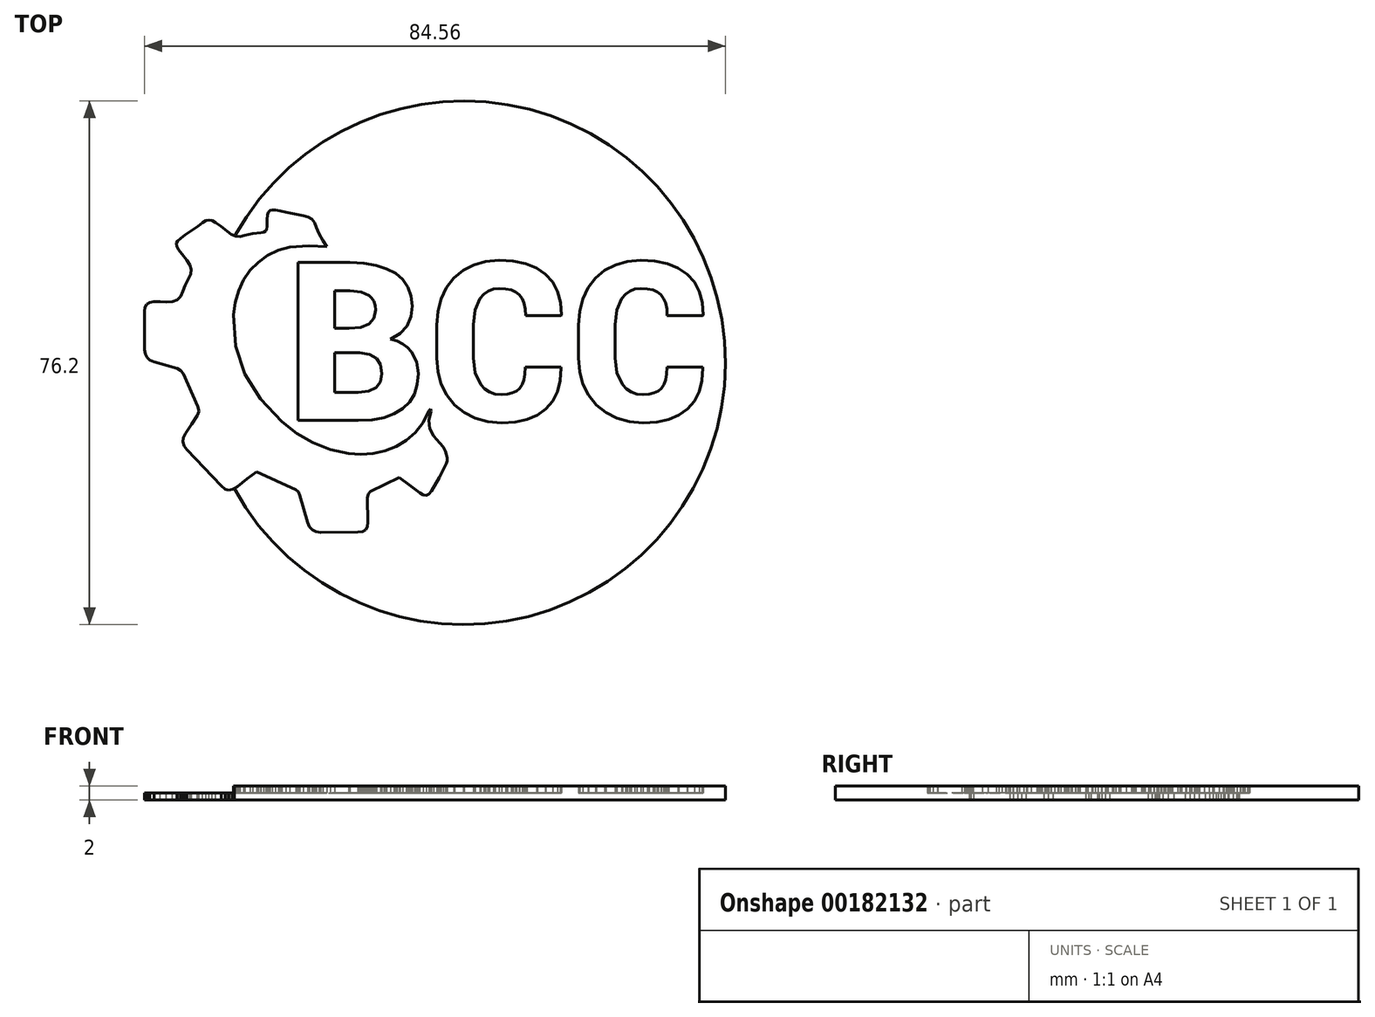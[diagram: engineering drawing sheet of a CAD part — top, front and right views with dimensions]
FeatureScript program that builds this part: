
annotation { "Feature Type Name" : "Feature", "Feature Type Description" : "" }
export const myFeature = defineFeature(function(context is Context, id is Id, definition is map)
    precondition{}
    {
        {
            var Q0;
            Q0=qCreatedBy(makeId("Top.planeOp"),FACE);
            var sketch = newSketch(context, id + "F0", { "sketchPlane" : qUnion([Q0])});
            skLineSegment(sketch, "E0", {"start": v(-30.18, -15.86) * mm, "end": v(-31.52, -16.9) * mm});
            skLineSegment(sketch, "E1", {"start": v(-31.52, -16.9) * mm, "end": v(-32.98, -18.03) * mm});
            skLineSegment(sketch, "E2", {"start": v(-32.98, -18.03) * mm, "end": v(-33.62, -18.42) * mm});
            skLineSegment(sketch, "E3", {"start": v(-33.62, -18.42) * mm, "end": v(-34.2, -18.54) * mm});
            skLineSegment(sketch, "E4", {"start": v(-34.2, -18.54) * mm, "end": v(-34.75, -18.38) * mm});
            skLineSegment(sketch, "E5", {"start": v(-34.75, -18.38) * mm, "end": v(-35.31, -17.92) * mm});
            skLineSegment(sketch, "E6", {"start": v(-35.31, -17.92) * mm, "end": v(-40.3, -12.66) * mm});
            skLineSegment(sketch, "E7", {"start": v(-40.3, -12.66) * mm, "end": v(-40.72, -12.09) * mm});
            skLineSegment(sketch, "E8", {"start": v(-40.72, -12.09) * mm, "end": v(-40.9, -11.5) * mm});
            skLineSegment(sketch, "E9", {"start": v(-40.9, -11.5) * mm, "end": v(-40.83, -10.89) * mm});
            skLineSegment(sketch, "E10", {"start": v(-40.83, -10.89) * mm, "end": v(-40.5, -10.25) * mm});
            skLineSegment(sketch, "E11", {"start": v(-40.5, -10.25) * mm, "end": v(-39.64, -8.96) * mm});
            skLineSegment(sketch, "E12", {"start": v(-39.64, -8.96) * mm, "end": v(-38.77, -7.68) * mm});
            skLineSegment(sketch, "E13", {"start": v(-38.77, -7.68) * mm, "end": v(-38.52, -7.03) * mm});
            skLineSegment(sketch, "E14", {"start": v(-38.52, -7.03) * mm, "end": v(-38.7, -6.34) * mm});
            skLineSegment(sketch, "E15", {"start": v(-38.7, -6.34) * mm, "end": v(-40.85, -1.59) * mm});
            skLineSegment(sketch, "E16", {"start": v(-40.85, -1.59) * mm, "end": v(-41.2, -1.1) * mm});
            skLineSegment(sketch, "E17", {"start": v(-41.2, -1.1) * mm, "end": v(-41.7, -0.8) * mm});
            skLineSegment(sketch, "E18", {"start": v(-41.7, -0.8) * mm, "end": v(-45.08, 0.16) * mm});
            skLineSegment(sketch, "E19", {"start": v(-45.08, 0.16) * mm, "end": v(-45.68, 0.41) * mm});
            skLineSegment(sketch, "E20", {"start": v(-45.68, 0.41) * mm, "end": v(-46.11, 0.8) * mm});
            skLineSegment(sketch, "E21", {"start": v(-46.11, 0.8) * mm, "end": v(-46.37, 1.3) * mm});
            skLineSegment(sketch, "E22", {"start": v(-46.37, 1.3) * mm, "end": v(-46.46, 1.94) * mm});
            skLineSegment(sketch, "E23", {"start": v(-46.46, 1.94) * mm, "end": v(-46.46, 7.49) * mm});
            skLineSegment(sketch, "E24", {"start": v(-46.46, 7.49) * mm, "end": v(-46.4, 8.09) * mm});
            skLineSegment(sketch, "E25", {"start": v(-46.4, 8.09) * mm, "end": v(-46.15, 8.53) * mm});
            skLineSegment(sketch, "E26", {"start": v(-46.15, 8.53) * mm, "end": v(-45.74, 8.8) * mm});
            skLineSegment(sketch, "E27", {"start": v(-45.74, 8.8) * mm, "end": v(-45.13, 8.9) * mm});
            skLineSegment(sketch, "E28", {"start": v(-45.13, 8.9) * mm, "end": v(-44.22, 8.87) * mm});
            skLineSegment(sketch, "E29", {"start": v(-44.22, 8.87) * mm, "end": v(-43.29, 8.83) * mm});
            skLineSegment(sketch, "E30", {"start": v(-43.29, 8.83) * mm, "end": v(-42.42, 8.88) * mm});
            skLineSegment(sketch, "E31", {"start": v(-42.42, 8.88) * mm, "end": v(-41.68, 9.15) * mm});
            skLineSegment(sketch, "E32", {"start": v(-41.68, 9.15) * mm, "end": v(-41.2, 9.68) * mm});
            skLineSegment(sketch, "E33", {"start": v(-41.2, 9.68) * mm, "end": v(-40.87, 10.4) * mm});
            skLineSegment(sketch, "E34", {"start": v(-40.87, 10.4) * mm, "end": v(-40.56, 11.26) * mm});
            skLineSegment(sketch, "E35", {"start": v(-40.56, 11.26) * mm, "end": v(-40.11, 12.14) * mm});
            skLineSegment(sketch, "E36", {"start": v(-40.11, 12.14) * mm, "end": v(-39.73, 12.92) * mm});
            skLineSegment(sketch, "E37", {"start": v(-39.73, 12.92) * mm, "end": v(-39.66, 13.6) * mm});
            skLineSegment(sketch, "E38", {"start": v(-39.66, 13.6) * mm, "end": v(-39.87, 14.23) * mm});
            skLineSegment(sketch, "E39", {"start": v(-39.87, 14.23) * mm, "end": v(-40.32, 14.9) * mm});
            skLineSegment(sketch, "E40", {"start": v(-40.32, 14.9) * mm, "end": v(-41.03, 15.81) * mm});
            skLineSegment(sketch, "E41", {"start": v(-41.03, 15.81) * mm, "end": v(-41.52, 16.49) * mm});
            skLineSegment(sketch, "E42", {"start": v(-41.52, 16.49) * mm, "end": v(-41.8, 16.99) * mm});
            skLineSegment(sketch, "E43", {"start": v(-41.8, 16.99) * mm, "end": v(-41.84, 17.38) * mm});
            skLineSegment(sketch, "E44", {"start": v(-41.84, 17.38) * mm, "end": v(-41.66, 17.74) * mm});
            skLineSegment(sketch, "E45", {"start": v(-41.66, 17.74) * mm, "end": v(-41.23, 18.12) * mm});
            skLineSegment(sketch, "E46", {"start": v(-41.23, 18.12) * mm, "end": v(-40.55, 18.6) * mm});
            skLineSegment(sketch, "E47", {"start": v(-40.55, 18.6) * mm, "end": v(-39.62, 19.23) * mm});
            skLineSegment(sketch, "E48", {"start": v(-39.62, 19.23) * mm, "end": v(-38.7, 19.89) * mm});
            skLineSegment(sketch, "E49", {"start": v(-38.7, 19.89) * mm, "end": v(-38.02, 20.38) * mm});
            skLineSegment(sketch, "E50", {"start": v(-38.02, 20.38) * mm, "end": v(-37.5, 20.68) * mm});
            skLineSegment(sketch, "E51", {"start": v(-37.5, 20.68) * mm, "end": v(-37.07, 20.8) * mm});
            skLineSegment(sketch, "E52", {"start": v(-37.07, 20.8) * mm, "end": v(-36.63, 20.7) * mm});
            skLineSegment(sketch, "E53", {"start": v(-36.63, 20.7) * mm, "end": v(-36.1, 20.4) * mm});
            skLineSegment(sketch, "E54", {"start": v(-36.1, 20.4) * mm, "end": v(-35.39, 19.87) * mm});
            skLineSegment(sketch, "E55", {"start": v(-35.39, 19.87) * mm, "end": v(-34.42, 19.1) * mm});
            skLineSegment(sketch, "E56", {"start": v(-34.42, 19.1) * mm, "end": v(-33.82, 18.69) * mm});
            skLineSegment(sketch, "E57", {"start": v(-33.82, 18.69) * mm, "end": v(-33.22, 18.43) * mm});
            skLineSegment(sketch, "E58", {"start": v(-33.22, 18.43) * mm, "end": v(-32.57, 18.37) * mm});
            skLineSegment(sketch, "E59", {"start": v(-32.57, 18.37) * mm, "end": v(-31.84, 18.55) * mm});
            skLineSegment(sketch, "E60", {"start": v(-31.84, 18.55) * mm, "end": v(-30.71, 18.83) * mm});
            skLineSegment(sketch, "E61", {"start": v(-30.71, 18.83) * mm, "end": v(-29.53, 18.94) * mm});
            skLineSegment(sketch, "E62", {"start": v(-29.53, 18.94) * mm, "end": v(-29.13, 19.01) * mm});
            skLineSegment(sketch, "E63", {"start": v(-29.13, 19.01) * mm, "end": v(-28.85, 19.18) * mm});
            skLineSegment(sketch, "E64", {"start": v(-28.85, 19.18) * mm, "end": v(-28.69, 19.45) * mm});
            skLineSegment(sketch, "E65", {"start": v(-28.69, 19.45) * mm, "end": v(-28.65, 19.84) * mm});
            skLineSegment(sketch, "E66", {"start": v(-28.65, 19.84) * mm, "end": v(-28.64, 19.95) * mm});
            skLineSegment(sketch, "E67", {"start": v(-28.64, 19.95) * mm, "end": v(-28.6, 20.86) * mm});
            skLineSegment(sketch, "E68", {"start": v(-28.6, 20.86) * mm, "end": v(-28.54, 21.5) * mm});
            skLineSegment(sketch, "E69", {"start": v(-28.54, 21.5) * mm, "end": v(-28.41, 21.94) * mm});
            skLineSegment(sketch, "E70", {"start": v(-28.41, 21.94) * mm, "end": v(-28.2, 22.18) * mm});
            skLineSegment(sketch, "E71", {"start": v(-28.2, 22.18) * mm, "end": v(-27.87, 22.26) * mm});
            skLineSegment(sketch, "E72", {"start": v(-27.87, 22.26) * mm, "end": v(-27.4, 22.22) * mm});
            skLineSegment(sketch, "E73", {"start": v(-27.4, 22.22) * mm, "end": v(-26.74, 22.1) * mm});
            skLineSegment(sketch, "E74", {"start": v(-26.74, 22.1) * mm, "end": v(-25.89, 21.9) * mm});
            skLineSegment(sketch, "E75", {"start": v(-25.89, 21.9) * mm, "end": v(-23.38, 21.4) * mm});
            skLineSegment(sketch, "E76", {"start": v(-23.38, 21.4) * mm, "end": v(-22.68, 21.21) * mm});
            skLineSegment(sketch, "E77", {"start": v(-22.68, 21.21) * mm, "end": v(-22.12, 20.88) * mm});
            skLineSegment(sketch, "E78", {"start": v(-22.12, 20.88) * mm, "end": v(-21.7, 20.4) * mm});
            skLineSegment(sketch, "E79", {"start": v(-21.7, 20.4) * mm, "end": v(-21.43, 19.71) * mm});
            skLineSegment(sketch, "E80", {"start": v(-21.43, 19.71) * mm, "end": v(-21.1, 18.81) * mm});
            skLineSegment(sketch, "E81", {"start": v(-21.1, 18.81) * mm, "end": v(-20.5, 17.81) * mm});
            skLineSegment(sketch, "E82", {"start": v(-20.5, 17.81) * mm, "end": v(-19.92, 16.9) * mm});
            skLineSegment(sketch, "E83", {"start": v(-19.92, 16.9) * mm, "end": v(-22.51, 17) * mm});
            skLineSegment(sketch, "E84", {"start": v(-22.51, 17) * mm, "end": v(-25.3, 16.84) * mm});
            skLineSegment(sketch, "E85", {"start": v(-25.3, 16.84) * mm, "end": v(-27, 16.36) * mm});
            skLineSegment(sketch, "E86", {"start": v(-27, 16.36) * mm, "end": v(-28.55, 15.62) * mm});
            skLineSegment(sketch, "E87", {"start": v(-28.55, 15.62) * mm, "end": v(-29.92, 14.64) * mm});
            skLineSegment(sketch, "E88", {"start": v(-29.92, 14.64) * mm, "end": v(-31.09, 13.44) * mm});
            skLineSegment(sketch, "E89", {"start": v(-31.09, 13.44) * mm, "end": v(-32.05, 12.05) * mm});
            skLineSegment(sketch, "E90", {"start": v(-32.05, 12.05) * mm, "end": v(-32.79, 10.5) * mm});
            skLineSegment(sketch, "E91", {"start": v(-32.79, 10.5) * mm, "end": v(-33.28, 8.8) * mm});
            skLineSegment(sketch, "E92", {"start": v(-33.28, 8.8) * mm, "end": v(-33.51, 6.97) * mm});
            skLineSegment(sketch, "E93", {"start": v(-33.51, 6.97) * mm, "end": v(-33.2, 2.44) * mm});
            skLineSegment(sketch, "E94", {"start": v(-33.2, 2.44) * mm, "end": v(-31.84, -1.63) * mm});
            skLineSegment(sketch, "E95", {"start": v(-31.84, -1.63) * mm, "end": v(-29.56, -5.27) * mm});
            skLineSegment(sketch, "E96", {"start": v(-29.56, -5.27) * mm, "end": v(-26.48, -8.55) * mm});
            skLineSegment(sketch, "E97", {"start": v(-26.48, -8.55) * mm, "end": v(-24.32, -10.27) * mm});
            skLineSegment(sketch, "E98", {"start": v(-24.32, -10.27) * mm, "end": v(-21.98, -11.63) * mm});
            skLineSegment(sketch, "E99", {"start": v(-21.98, -11.63) * mm, "end": v(-19.45, -12.63) * mm});
            skLineSegment(sketch, "E100", {"start": v(-19.45, -12.63) * mm, "end": v(-16.73, -13.23) * mm});
            skLineSegment(sketch, "E101", {"start": v(-16.73, -13.23) * mm, "end": v(-14.95, -13.35) * mm});
            skLineSegment(sketch, "E102", {"start": v(-14.95, -13.35) * mm, "end": v(-13.19, -13.22) * mm});
            skLineSegment(sketch, "E103", {"start": v(-13.19, -13.22) * mm, "end": v(-11.48, -12.83) * mm});
            skLineSegment(sketch, "E104", {"start": v(-11.48, -12.83) * mm, "end": v(-9.86, -12.2) * mm});
            skLineSegment(sketch, "E105", {"start": v(-9.86, -12.2) * mm, "end": v(-8.37, -11.29) * mm});
            skLineSegment(sketch, "E106", {"start": v(-8.37, -11.29) * mm, "end": v(-7.04, -10.13) * mm});
            skLineSegment(sketch, "E107", {"start": v(-7.04, -10.13) * mm, "end": v(-5.92, -8.7) * mm});
            skLineSegment(sketch, "E108", {"start": v(-5.92, -8.7) * mm, "end": v(-5.04, -7) * mm});
            skLineSegment(sketch, "E109", {"start": v(-5.04, -7) * mm, "end": v(-4.8, -6.73) * mm});
            skLineSegment(sketch, "E110", {"start": v(-4.8, -6.73) * mm, "end": v(-4.76, -7.05) * mm});
            skLineSegment(sketch, "E111", {"start": v(-4.76, -7.05) * mm, "end": v(-5.06, -8.37) * mm});
            skLineSegment(sketch, "E112", {"start": v(-5.06, -8.37) * mm, "end": v(-4.92, -9.58) * mm});
            skLineSegment(sketch, "E113", {"start": v(-4.92, -9.58) * mm, "end": v(-4.4, -10.68) * mm});
            skLineSegment(sketch, "E114", {"start": v(-4.4, -10.68) * mm, "end": v(-3.51, -11.7) * mm});
            skLineSegment(sketch, "E115", {"start": v(-3.51, -11.7) * mm, "end": v(-3, -12.25) * mm});
            skLineSegment(sketch, "E116", {"start": v(-3, -12.25) * mm, "end": v(-2.63, -12.89) * mm});
            skLineSegment(sketch, "E117", {"start": v(-2.63, -12.89) * mm, "end": v(-2.5, -13.33) * mm});
            skLineSegment(sketch, "E118", {"start": v(-2.5, -13.33) * mm, "end": v(-2.41, -13.8) * mm});
            skLineSegment(sketch, "E119", {"start": v(-2.41, -13.8) * mm, "end": v(-2.4, -14.26) * mm});
            skLineSegment(sketch, "E120", {"start": v(-2.4, -14.26) * mm, "end": v(-2.5, -14.66) * mm});
            skLineSegment(sketch, "E121", {"start": v(-2.5, -14.66) * mm, "end": v(-3.56, -16.68) * mm});
            skLineSegment(sketch, "E122", {"start": v(-3.56, -16.68) * mm, "end": v(-4.71, -18.67) * mm});
            skLineSegment(sketch, "E123", {"start": v(-4.71, -18.67) * mm, "end": v(-5.07, -19.12) * mm});
            skLineSegment(sketch, "E124", {"start": v(-5.07, -19.12) * mm, "end": v(-5.47, -19.3) * mm});
            skLineSegment(sketch, "E125", {"start": v(-5.47, -19.3) * mm, "end": v(-5.9, -19.23) * mm});
            skLineSegment(sketch, "E126", {"start": v(-5.9, -19.23) * mm, "end": v(-6.38, -18.95) * mm});
            skLineSegment(sketch, "E127", {"start": v(-6.38, -18.95) * mm, "end": v(-7.94, -17.77) * mm});
            skLineSegment(sketch, "E128", {"start": v(-7.94, -17.77) * mm, "end": v(-9.41, -16.66) * mm});
            skLineSegment(sketch, "E129", {"start": v(-9.41, -16.66) * mm, "end": v(-13.58, -18.74) * mm});
            skLineSegment(sketch, "E130", {"start": v(-13.58, -18.74) * mm, "end": v(-13.9, -19.12) * mm});
            skLineSegment(sketch, "E131", {"start": v(-13.9, -19.12) * mm, "end": v(-14.03, -19.65) * mm});
            skLineSegment(sketch, "E132", {"start": v(-14.03, -19.65) * mm, "end": v(-13.95, -23.16) * mm});
            skLineSegment(sketch, "E133", {"start": v(-13.95, -23.16) * mm, "end": v(-14.02, -23.86) * mm});
            skLineSegment(sketch, "E134", {"start": v(-14.02, -23.86) * mm, "end": v(-14.26, -24.32) * mm});
            skLineSegment(sketch, "E135", {"start": v(-14.26, -24.32) * mm, "end": v(-14.71, -24.58) * mm});
            skLineSegment(sketch, "E136", {"start": v(-14.71, -24.58) * mm, "end": v(-15.4, -24.66) * mm});
            skLineSegment(sketch, "E137", {"start": v(-15.4, -24.66) * mm, "end": v(-20.84, -24.66) * mm});
            skLineSegment(sketch, "E138", {"start": v(-20.84, -24.66) * mm, "end": v(-21.52, -24.58) * mm});
            skLineSegment(sketch, "E139", {"start": v(-21.52, -24.58) * mm, "end": v(-22.05, -24.32) * mm});
            skLineSegment(sketch, "E140", {"start": v(-22.05, -24.32) * mm, "end": v(-22.45, -23.88) * mm});
            skLineSegment(sketch, "E141", {"start": v(-22.45, -23.88) * mm, "end": v(-22.71, -23.26) * mm});
            skLineSegment(sketch, "E142", {"start": v(-22.71, -23.26) * mm, "end": v(-23.86, -19.26) * mm});
            skLineSegment(sketch, "E143", {"start": v(-23.86, -19.26) * mm, "end": v(-24.09, -18.8) * mm});
            skLineSegment(sketch, "E144", {"start": v(-24.09, -18.8) * mm, "end": v(-24.44, -18.48) * mm});
            skLineSegment(sketch, "E145", {"start": v(-24.44, -18.48) * mm, "end": v(-30.18, -15.86) * mm});
            skLineSegment(sketch, "E146", {"start": v(-18.77, 1.47) * mm, "end": v(-18.77, -4.3) * mm});
            skLineSegment(sketch, "E147", {"start": v(-18.77, -4.3) * mm, "end": v(-15.34, -4.3) * mm});
            skLineSegment(sketch, "E148", {"start": v(-15.34, -4.3) * mm, "end": v(-13.85, -4.12) * mm});
            skLineSegment(sketch, "E149", {"start": v(-13.85, -4.12) * mm, "end": v(-12.78, -3.62) * mm});
            skLineSegment(sketch, "E150", {"start": v(-12.78, -3.62) * mm, "end": v(-12.15, -2.77) * mm});
            skLineSegment(sketch, "E151", {"start": v(-12.15, -2.77) * mm, "end": v(-11.93, -1.56) * mm});
            skLineSegment(sketch, "E152", {"start": v(-11.93, -1.56) * mm, "end": v(-12.12, -0.27) * mm});
            skLineSegment(sketch, "E153", {"start": v(-12.12, -0.27) * mm, "end": v(-12.68, 0.66) * mm});
            skLineSegment(sketch, "E154", {"start": v(-12.68, 0.66) * mm, "end": v(-13.67, 1.24) * mm});
            skLineSegment(sketch, "E155", {"start": v(-13.67, 1.24) * mm, "end": v(-15.15, 1.47) * mm});
            skLineSegment(sketch, "E156", {"start": v(-15.15, 1.47) * mm, "end": v(-15.33, 1.47) * mm});
            skLineSegment(sketch, "E157", {"start": v(-15.33, 1.47) * mm, "end": v(-18.77, 1.47) * mm});
            skLineSegment(sketch, "E158", {"start": v(-18.77, 5) * mm, "end": v(-16.67, 5) * mm});
            skLineSegment(sketch, "E159", {"start": v(-16.67, 5) * mm, "end": v(-14.99, 5.17) * mm});
            skLineSegment(sketch, "E160", {"start": v(-14.99, 5.17) * mm, "end": v(-13.8, 5.67) * mm});
            skLineSegment(sketch, "E161", {"start": v(-13.8, 5.67) * mm, "end": v(-13.08, 6.5) * mm});
            skLineSegment(sketch, "E162", {"start": v(-13.08, 6.5) * mm, "end": v(-12.85, 7.67) * mm});
            skLineSegment(sketch, "E163", {"start": v(-12.85, 7.67) * mm, "end": v(-12.9, 8.36) * mm});
            skLineSegment(sketch, "E164", {"start": v(-12.9, 8.36) * mm, "end": v(-13.08, 8.94) * mm});
            skLineSegment(sketch, "E165", {"start": v(-13.08, 8.94) * mm, "end": v(-13.36, 9.43) * mm});
            skLineSegment(sketch, "E166", {"start": v(-13.36, 9.43) * mm, "end": v(-13.76, 9.8) * mm});
            skLineSegment(sketch, "E167", {"start": v(-13.76, 9.8) * mm, "end": v(-14.92, 10.31) * mm});
            skLineSegment(sketch, "E168", {"start": v(-14.92, 10.31) * mm, "end": v(-16.57, 10.48) * mm});
            skLineSegment(sketch, "E169", {"start": v(-16.57, 10.48) * mm, "end": v(-18.77, 10.48) * mm});
            skLineSegment(sketch, "E170", {"start": v(-18.77, 10.48) * mm, "end": v(-18.77, 5) * mm});
            skLineSegment(sketch, "E171", {"start": v(-24.1, -8.4) * mm, "end": v(-24.1, 14.58) * mm});
            skLineSegment(sketch, "E172", {"start": v(-24.1, 14.58) * mm, "end": v(-16.57, 14.58) * mm});
            skLineSegment(sketch, "E173", {"start": v(-16.57, 14.58) * mm, "end": v(-14.55, 14.49) * mm});
            skLineSegment(sketch, "E174", {"start": v(-14.55, 14.49) * mm, "end": v(-12.77, 14.19) * mm});
            skLineSegment(sketch, "E175", {"start": v(-12.77, 14.19) * mm, "end": v(-11.22, 13.7) * mm});
            skLineSegment(sketch, "E176", {"start": v(-11.22, 13.7) * mm, "end": v(-9.9, 13) * mm});
            skLineSegment(sketch, "E177", {"start": v(-9.9, 13) * mm, "end": v(-8.86, 12.1) * mm});
            skLineSegment(sketch, "E178", {"start": v(-8.86, 12.1) * mm, "end": v(-8.11, 11.02) * mm});
            skLineSegment(sketch, "E179", {"start": v(-8.11, 11.02) * mm, "end": v(-7.66, 9.74) * mm});
            skLineSegment(sketch, "E180", {"start": v(-7.66, 9.74) * mm, "end": v(-7.51, 8.27) * mm});
            skLineSegment(sketch, "E181", {"start": v(-7.51, 8.27) * mm, "end": v(-7.7, 6.72) * mm});
            skLineSegment(sketch, "E182", {"start": v(-7.7, 6.72) * mm, "end": v(-8.27, 5.36) * mm});
            skLineSegment(sketch, "E183", {"start": v(-8.27, 5.36) * mm, "end": v(-9.24, 4.24) * mm});
            skLineSegment(sketch, "E184", {"start": v(-9.24, 4.24) * mm, "end": v(-10.64, 3.44) * mm});
            skLineSegment(sketch, "E185", {"start": v(-10.64, 3.44) * mm, "end": v(-9.68, 3.16) * mm});
            skLineSegment(sketch, "E186", {"start": v(-9.68, 3.16) * mm, "end": v(-8.85, 2.76) * mm});
            skLineSegment(sketch, "E187", {"start": v(-8.85, 2.76) * mm, "end": v(-8.16, 2.25) * mm});
            skLineSegment(sketch, "E188", {"start": v(-8.16, 2.25) * mm, "end": v(-7.6, 1.61) * mm});
            skLineSegment(sketch, "E189", {"start": v(-7.6, 1.61) * mm, "end": v(-6.86, 0.12) * mm});
            skLineSegment(sketch, "E190", {"start": v(-6.86, 0.12) * mm, "end": v(-6.61, -1.6) * mm});
            skLineSegment(sketch, "E191", {"start": v(-6.61, -1.6) * mm, "end": v(-6.75, -3.17) * mm});
            skLineSegment(sketch, "E192", {"start": v(-6.75, -3.17) * mm, "end": v(-7.18, -4.54) * mm});
            skLineSegment(sketch, "E193", {"start": v(-7.18, -4.54) * mm, "end": v(-7.88, -5.71) * mm});
            skLineSegment(sketch, "E194", {"start": v(-7.88, -5.71) * mm, "end": v(-8.87, -6.68) * mm});
            skLineSegment(sketch, "E195", {"start": v(-8.87, -6.68) * mm, "end": v(-10.12, -7.43) * mm});
            skLineSegment(sketch, "E196", {"start": v(-10.12, -7.43) * mm, "end": v(-11.62, -7.97) * mm});
            skLineSegment(sketch, "E197", {"start": v(-11.62, -7.97) * mm, "end": v(-13.36, -8.29) * mm});
            skLineSegment(sketch, "E198", {"start": v(-13.36, -8.29) * mm, "end": v(-15.34, -8.4) * mm});
            skLineSegment(sketch, "E199", {"start": v(-15.34, -8.4) * mm, "end": v(-24.1, -8.4) * mm});
            skLineSegment(sketch, "E200", {"start": v(14.16, -0.65) * mm, "end": v(14.19, -0.74) * mm});
            skLineSegment(sketch, "E201", {"start": v(14.19, -0.74) * mm, "end": v(14.07, -2.59) * mm});
            skLineSegment(sketch, "E202", {"start": v(14.07, -2.59) * mm, "end": v(13.67, -4.2) * mm});
            skLineSegment(sketch, "E203", {"start": v(13.67, -4.2) * mm, "end": v(12.96, -5.57) * mm});
            skLineSegment(sketch, "E204", {"start": v(12.96, -5.57) * mm, "end": v(11.97, -6.7) * mm});
            skLineSegment(sketch, "E205", {"start": v(11.97, -6.7) * mm, "end": v(10.71, -7.59) * mm});
            skLineSegment(sketch, "E206", {"start": v(10.71, -7.59) * mm, "end": v(9.21, -8.22) * mm});
            skLineSegment(sketch, "E207", {"start": v(9.21, -8.22) * mm, "end": v(7.48, -8.6) * mm});
            skLineSegment(sketch, "E208", {"start": v(7.48, -8.6) * mm, "end": v(5.5, -8.73) * mm});
            skLineSegment(sketch, "E209", {"start": v(5.5, -8.73) * mm, "end": v(3.48, -8.56) * mm});
            skLineSegment(sketch, "E210", {"start": v(3.48, -8.56) * mm, "end": v(1.67, -8.08) * mm});
            skLineSegment(sketch, "E211", {"start": v(1.67, -8.08) * mm, "end": v(0.06, -7.26) * mm});
            skLineSegment(sketch, "E212", {"start": v(0.06, -7.26) * mm, "end": v(-1.33, -6.12) * mm});
            skLineSegment(sketch, "E213", {"start": v(-1.33, -6.12) * mm, "end": v(-2.46, -4.72) * mm});
            skLineSegment(sketch, "E214", {"start": v(-2.46, -4.72) * mm, "end": v(-3.27, -3.12) * mm});
            skLineSegment(sketch, "E215", {"start": v(-3.27, -3.12) * mm, "end": v(-3.75, -1.31) * mm});
            skLineSegment(sketch, "E216", {"start": v(-3.75, -1.31) * mm, "end": v(-3.91, 0.7) * mm});
            skLineSegment(sketch, "E217", {"start": v(-3.91, 0.7) * mm, "end": v(-3.91, 5.5) * mm});
            skLineSegment(sketch, "E218", {"start": v(-3.91, 5.5) * mm, "end": v(-3.76, 7.5) * mm});
            skLineSegment(sketch, "E219", {"start": v(-3.76, 7.5) * mm, "end": v(-3.3, 9.3) * mm});
            skLineSegment(sketch, "E220", {"start": v(-3.3, 9.3) * mm, "end": v(-2.52, 10.9) * mm});
            skLineSegment(sketch, "E221", {"start": v(-2.52, 10.9) * mm, "end": v(-1.43, 12.3) * mm});
            skLineSegment(sketch, "E222", {"start": v(-1.43, 12.3) * mm, "end": v(-0.09, 13.45) * mm});
            skLineSegment(sketch, "E223", {"start": v(-0.09, 13.45) * mm, "end": v(1.46, 14.26) * mm});
            skLineSegment(sketch, "E224", {"start": v(1.46, 14.26) * mm, "end": v(3.2, 14.75) * mm});
            skLineSegment(sketch, "E225", {"start": v(3.2, 14.75) * mm, "end": v(5.15, 14.92) * mm});
            skLineSegment(sketch, "E226", {"start": v(5.15, 14.92) * mm, "end": v(7.2, 14.79) * mm});
            skLineSegment(sketch, "E227", {"start": v(7.2, 14.79) * mm, "end": v(9.02, 14.4) * mm});
            skLineSegment(sketch, "E228", {"start": v(9.02, 14.4) * mm, "end": v(10.59, 13.77) * mm});
            skLineSegment(sketch, "E229", {"start": v(10.59, 13.77) * mm, "end": v(11.9, 12.88) * mm});
            skLineSegment(sketch, "E230", {"start": v(11.9, 12.88) * mm, "end": v(12.95, 11.75) * mm});
            skLineSegment(sketch, "E231", {"start": v(12.95, 11.75) * mm, "end": v(13.69, 10.38) * mm});
            skLineSegment(sketch, "E232", {"start": v(13.69, 10.38) * mm, "end": v(14.11, 8.79) * mm});
            skLineSegment(sketch, "E233", {"start": v(14.11, 8.79) * mm, "end": v(14.24, 6.96) * mm});
            skLineSegment(sketch, "E234", {"start": v(14.24, 6.96) * mm, "end": v(14.19, 6.87) * mm});
            skLineSegment(sketch, "E235", {"start": v(14.19, 6.87) * mm, "end": v(9, 6.87) * mm});
            skLineSegment(sketch, "E236", {"start": v(9, 6.87) * mm, "end": v(8.94, 7.85) * mm});
            skLineSegment(sketch, "E237", {"start": v(8.94, 7.85) * mm, "end": v(8.77, 8.68) * mm});
            skLineSegment(sketch, "E238", {"start": v(8.77, 8.68) * mm, "end": v(8.49, 9.36) * mm});
            skLineSegment(sketch, "E239", {"start": v(8.49, 9.36) * mm, "end": v(8.1, 9.9) * mm});
            skLineSegment(sketch, "E240", {"start": v(8.1, 9.9) * mm, "end": v(7.57, 10.3) * mm});
            skLineSegment(sketch, "E241", {"start": v(7.57, 10.3) * mm, "end": v(6.9, 10.58) * mm});
            skLineSegment(sketch, "E242", {"start": v(6.9, 10.58) * mm, "end": v(6.1, 10.75) * mm});
            skLineSegment(sketch, "E243", {"start": v(6.1, 10.75) * mm, "end": v(5.15, 10.81) * mm});
            skLineSegment(sketch, "E244", {"start": v(5.15, 10.81) * mm, "end": v(4.3, 10.72) * mm});
            skLineSegment(sketch, "E245", {"start": v(4.3, 10.72) * mm, "end": v(3.55, 10.45) * mm});
            skLineSegment(sketch, "E246", {"start": v(3.55, 10.45) * mm, "end": v(2.92, 10) * mm});
            skLineSegment(sketch, "E247", {"start": v(2.92, 10) * mm, "end": v(2.38, 9.37) * mm});
            skLineSegment(sketch, "E248", {"start": v(2.38, 9.37) * mm, "end": v(1.66, 7.69) * mm});
            skLineSegment(sketch, "E249", {"start": v(1.66, 7.69) * mm, "end": v(1.42, 5.52) * mm});
            skLineSegment(sketch, "E250", {"start": v(1.42, 5.52) * mm, "end": v(1.42, 0.7) * mm});
            skLineSegment(sketch, "E251", {"start": v(1.42, 0.7) * mm, "end": v(1.68, -1.48) * mm});
            skLineSegment(sketch, "E252", {"start": v(1.68, -1.48) * mm, "end": v(2.48, -3.17) * mm});
            skLineSegment(sketch, "E253", {"start": v(2.48, -3.17) * mm, "end": v(3.06, -3.8) * mm});
            skLineSegment(sketch, "E254", {"start": v(3.06, -3.8) * mm, "end": v(3.76, -4.26) * mm});
            skLineSegment(sketch, "E255", {"start": v(3.76, -4.26) * mm, "end": v(4.58, -4.53) * mm});
            skLineSegment(sketch, "E256", {"start": v(4.58, -4.53) * mm, "end": v(5.5, -4.62) * mm});
            skLineSegment(sketch, "E257", {"start": v(5.5, -4.62) * mm, "end": v(6.36, -4.57) * mm});
            skLineSegment(sketch, "E258", {"start": v(6.36, -4.57) * mm, "end": v(7.08, -4.4) * mm});
            skLineSegment(sketch, "E259", {"start": v(7.08, -4.4) * mm, "end": v(7.68, -4.1) * mm});
            skLineSegment(sketch, "E260", {"start": v(7.68, -4.1) * mm, "end": v(8.15, -3.7) * mm});
            skLineSegment(sketch, "E261", {"start": v(8.15, -3.7) * mm, "end": v(8.5, -3.17) * mm});
            skLineSegment(sketch, "E262", {"start": v(8.5, -3.17) * mm, "end": v(8.76, -2.49) * mm});
            skLineSegment(sketch, "E263", {"start": v(8.76, -2.49) * mm, "end": v(8.91, -1.64) * mm});
            skLineSegment(sketch, "E264", {"start": v(8.91, -1.64) * mm, "end": v(8.96, -0.65) * mm});
            skLineSegment(sketch, "E265", {"start": v(8.96, -0.65) * mm, "end": v(14.16, -0.65) * mm});
            skLineSegment(sketch, "E266", {"start": v(34.79, -0.65) * mm, "end": v(34.82, -0.74) * mm});
            skLineSegment(sketch, "E267", {"start": v(34.82, -0.74) * mm, "end": v(34.7, -2.59) * mm});
            skLineSegment(sketch, "E268", {"start": v(34.7, -2.59) * mm, "end": v(34.3, -4.2) * mm});
            skLineSegment(sketch, "E269", {"start": v(34.3, -4.2) * mm, "end": v(33.6, -5.57) * mm});
            skLineSegment(sketch, "E270", {"start": v(33.6, -5.57) * mm, "end": v(32.6, -6.7) * mm});
            skLineSegment(sketch, "E271", {"start": v(32.6, -6.7) * mm, "end": v(31.34, -7.59) * mm});
            skLineSegment(sketch, "E272", {"start": v(31.34, -7.59) * mm, "end": v(29.84, -8.22) * mm});
            skLineSegment(sketch, "E273", {"start": v(29.84, -8.22) * mm, "end": v(28.1, -8.6) * mm});
            skLineSegment(sketch, "E274", {"start": v(28.1, -8.6) * mm, "end": v(26.14, -8.73) * mm});
            skLineSegment(sketch, "E275", {"start": v(26.14, -8.73) * mm, "end": v(24.11, -8.56) * mm});
            skLineSegment(sketch, "E276", {"start": v(24.11, -8.56) * mm, "end": v(22.3, -8.08) * mm});
            skLineSegment(sketch, "E277", {"start": v(22.3, -8.08) * mm, "end": v(20.69, -7.26) * mm});
            skLineSegment(sketch, "E278", {"start": v(20.69, -7.26) * mm, "end": v(19.3, -6.12) * mm});
            skLineSegment(sketch, "E279", {"start": v(19.3, -6.12) * mm, "end": v(18.17, -4.72) * mm});
            skLineSegment(sketch, "E280", {"start": v(18.17, -4.72) * mm, "end": v(17.36, -3.12) * mm});
            skLineSegment(sketch, "E281", {"start": v(17.36, -3.12) * mm, "end": v(16.87, -1.31) * mm});
            skLineSegment(sketch, "E282", {"start": v(16.87, -1.31) * mm, "end": v(16.71, 0.7) * mm});
            skLineSegment(sketch, "E283", {"start": v(16.71, 0.7) * mm, "end": v(16.71, 5.5) * mm});
            skLineSegment(sketch, "E284", {"start": v(16.71, 5.5) * mm, "end": v(16.87, 7.5) * mm});
            skLineSegment(sketch, "E285", {"start": v(16.87, 7.5) * mm, "end": v(17.34, 9.3) * mm});
            skLineSegment(sketch, "E286", {"start": v(17.34, 9.3) * mm, "end": v(18.11, 10.9) * mm});
            skLineSegment(sketch, "E287", {"start": v(18.11, 10.9) * mm, "end": v(19.2, 12.3) * mm});
            skLineSegment(sketch, "E288", {"start": v(19.2, 12.3) * mm, "end": v(20.54, 13.45) * mm});
            skLineSegment(sketch, "E289", {"start": v(20.54, 13.45) * mm, "end": v(22.09, 14.26) * mm});
            skLineSegment(sketch, "E290", {"start": v(22.09, 14.26) * mm, "end": v(23.83, 14.75) * mm});
            skLineSegment(sketch, "E291", {"start": v(23.83, 14.75) * mm, "end": v(25.77, 14.92) * mm});
            skLineSegment(sketch, "E292", {"start": v(25.77, 14.92) * mm, "end": v(27.84, 14.79) * mm});
            skLineSegment(sketch, "E293", {"start": v(27.84, 14.79) * mm, "end": v(29.65, 14.4) * mm});
            skLineSegment(sketch, "E294", {"start": v(29.65, 14.4) * mm, "end": v(31.22, 13.77) * mm});
            skLineSegment(sketch, "E295", {"start": v(31.22, 13.77) * mm, "end": v(32.54, 12.88) * mm});
            skLineSegment(sketch, "E296", {"start": v(32.54, 12.88) * mm, "end": v(33.58, 11.75) * mm});
            skLineSegment(sketch, "E297", {"start": v(33.58, 11.75) * mm, "end": v(34.31, 10.38) * mm});
            skLineSegment(sketch, "E298", {"start": v(34.31, 10.38) * mm, "end": v(34.74, 8.79) * mm});
            skLineSegment(sketch, "E299", {"start": v(34.74, 8.79) * mm, "end": v(34.86, 6.96) * mm});
            skLineSegment(sketch, "E300", {"start": v(34.86, 6.96) * mm, "end": v(34.82, 6.87) * mm});
            skLineSegment(sketch, "E301", {"start": v(34.82, 6.87) * mm, "end": v(29.62, 6.87) * mm});
            skLineSegment(sketch, "E302", {"start": v(29.62, 6.87) * mm, "end": v(29.57, 7.85) * mm});
            skLineSegment(sketch, "E303", {"start": v(29.57, 7.85) * mm, "end": v(29.4, 8.68) * mm});
            skLineSegment(sketch, "E304", {"start": v(29.4, 8.68) * mm, "end": v(29.12, 9.36) * mm});
            skLineSegment(sketch, "E305", {"start": v(29.12, 9.36) * mm, "end": v(28.73, 9.9) * mm});
            skLineSegment(sketch, "E306", {"start": v(28.73, 9.9) * mm, "end": v(28.2, 10.3) * mm});
            skLineSegment(sketch, "E307", {"start": v(28.2, 10.3) * mm, "end": v(27.54, 10.58) * mm});
            skLineSegment(sketch, "E308", {"start": v(27.54, 10.58) * mm, "end": v(26.73, 10.75) * mm});
            skLineSegment(sketch, "E309", {"start": v(26.73, 10.75) * mm, "end": v(25.77, 10.81) * mm});
            skLineSegment(sketch, "E310", {"start": v(25.77, 10.81) * mm, "end": v(24.93, 10.72) * mm});
            skLineSegment(sketch, "E311", {"start": v(24.93, 10.72) * mm, "end": v(24.18, 10.45) * mm});
            skLineSegment(sketch, "E312", {"start": v(24.18, 10.45) * mm, "end": v(23.54, 10) * mm});
            skLineSegment(sketch, "E313", {"start": v(23.54, 10) * mm, "end": v(23.01, 9.37) * mm});
            skLineSegment(sketch, "E314", {"start": v(23.01, 9.37) * mm, "end": v(22.29, 7.69) * mm});
            skLineSegment(sketch, "E315", {"start": v(22.29, 7.69) * mm, "end": v(22.05, 5.52) * mm});
            skLineSegment(sketch, "E316", {"start": v(22.05, 5.52) * mm, "end": v(22.05, 0.7) * mm});
            skLineSegment(sketch, "E317", {"start": v(22.05, 0.7) * mm, "end": v(22.31, -1.48) * mm});
            skLineSegment(sketch, "E318", {"start": v(22.31, -1.48) * mm, "end": v(23.1, -3.17) * mm});
            skLineSegment(sketch, "E319", {"start": v(23.1, -3.17) * mm, "end": v(23.7, -3.8) * mm});
            skLineSegment(sketch, "E320", {"start": v(23.7, -3.8) * mm, "end": v(24.4, -4.26) * mm});
            skLineSegment(sketch, "E321", {"start": v(24.4, -4.26) * mm, "end": v(25.2, -4.53) * mm});
            skLineSegment(sketch, "E322", {"start": v(25.2, -4.53) * mm, "end": v(26.14, -4.62) * mm});
            skLineSegment(sketch, "E323", {"start": v(26.14, -4.62) * mm, "end": v(26.99, -4.57) * mm});
            skLineSegment(sketch, "E324", {"start": v(26.99, -4.57) * mm, "end": v(27.71, -4.4) * mm});
            skLineSegment(sketch, "E325", {"start": v(27.71, -4.4) * mm, "end": v(28.31, -4.1) * mm});
            skLineSegment(sketch, "E326", {"start": v(28.31, -4.1) * mm, "end": v(28.78, -3.7) * mm});
            skLineSegment(sketch, "E327", {"start": v(28.78, -3.7) * mm, "end": v(29.14, -3.17) * mm});
            skLineSegment(sketch, "E328", {"start": v(29.14, -3.17) * mm, "end": v(29.39, -2.49) * mm});
            skLineSegment(sketch, "E329", {"start": v(29.39, -2.49) * mm, "end": v(29.54, -1.64) * mm});
            skLineSegment(sketch, "E330", {"start": v(29.54, -1.64) * mm, "end": v(29.6, -0.65) * mm});
            skLineSegment(sketch, "E331", {"start": v(29.6, -0.65) * mm, "end": v(34.79, -0.65) * mm});
            skSolve(sketch);
        }
        {
            var Q0;
            Q0=qCreatedBy(makeId("Top.planeOp"),FACE);
            var sketch = newSketch(context, id + "F1", { "sketchPlane" : qUnion([Q0])});
            skCircle(sketch, "E332", {"center": v(0, 0) * mm, "radius": 38.1 * mm});
            skSolve(sketch);
        }
        {
            var Q0;
            Q0 = qSketchRegion(id + "F1", true);
            extrude(context, id + "F2", {"entities" : qUnion([Q0]), "depth" : 1 * mm, "offsetDistance" : 25 * mm});
        }
        {
            var Q0;
            Q0 = qSketchRegion(id + "F0", true);
            extrude(context, id + "F3", {"entities" : qUnion([Q0]), "operationType" : NewBodyOperationType.REMOVE, "depth" : 25 * mm});
        }
        {
            var Q0;
            Q0 = qSketchRegion(id + "F0", true);
            extrude(context, id + "F4", {"entities" : qUnion([Q0]), "oppositeDirection" : true, "depth" : 1 * mm});
        }
        {
            var Q0;
            Q0 = qSketchRegion(id + "F1", true);
            extrude(context, id + "F5", {"entities" : qUnion([Q0]), "operationType" : NewBodyOperationType.REMOVE, "oppositeDirection" : true, "depth" : 25 * mm});
        }
        {
            var Q0;
            Q0 = qSketchRegion(id + "F1", true);
            extrude(context, id + "F6", {"entities" : qUnion([Q0]), "operationType" : NewBodyOperationType.ADD, "oppositeDirection" : true, "depth" : 1 * mm});
        }
    });
